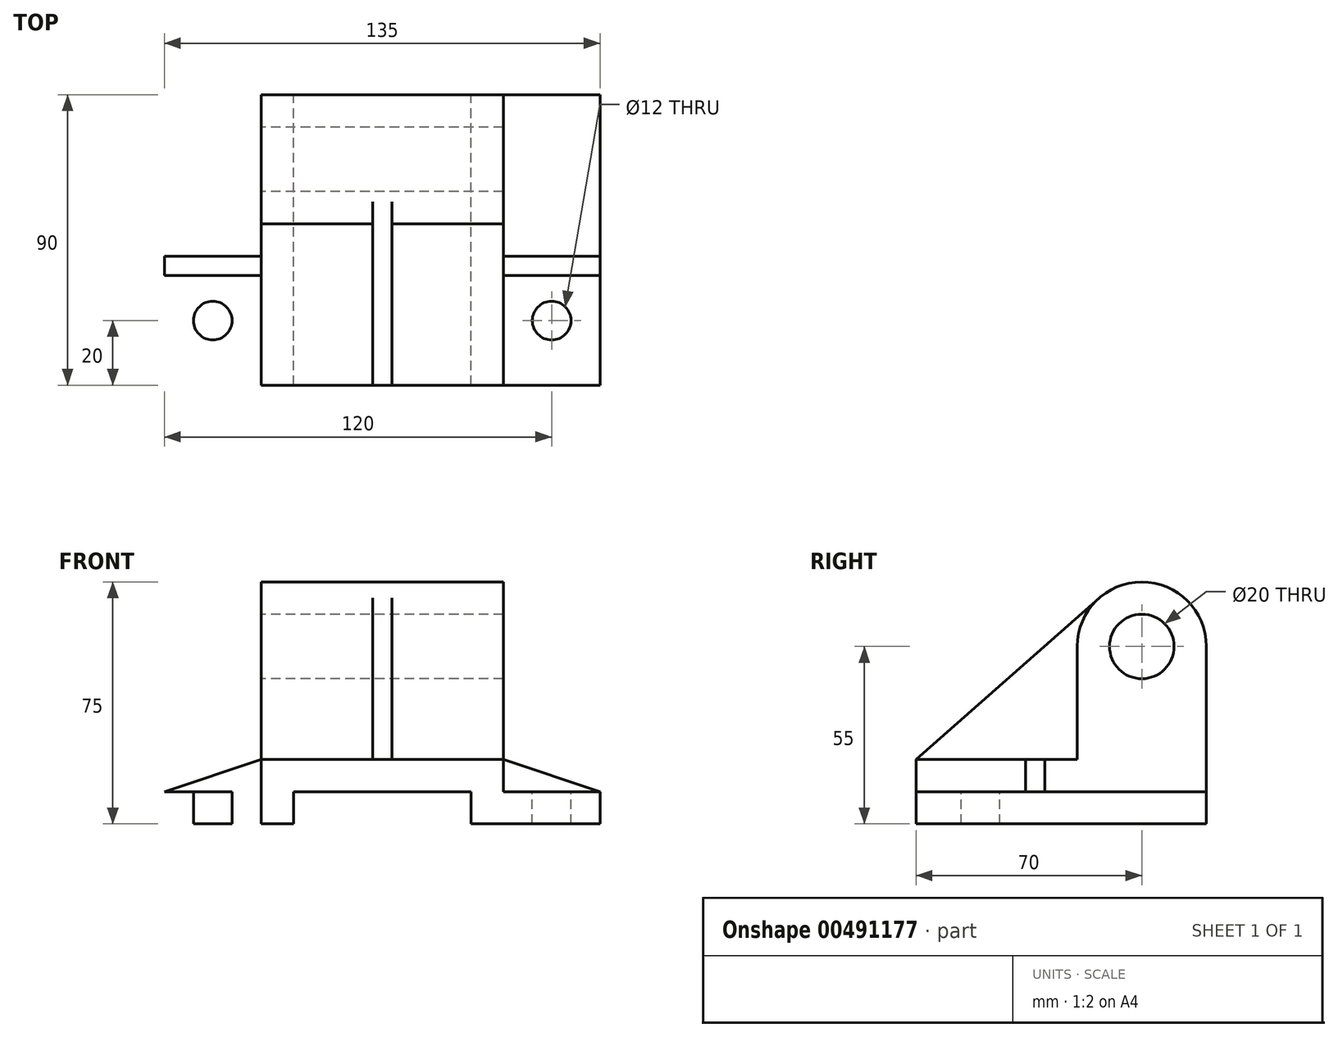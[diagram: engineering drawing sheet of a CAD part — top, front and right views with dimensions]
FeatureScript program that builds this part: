
annotation { "Feature Type Name" : "Feature", "Feature Type Description" : "" }
export const myFeature = defineFeature(function(context is Context, id is Id, definition is map)
    precondition{}
    {
        {
            var Q0;
            Q0=qCreatedBy(makeId("Front.planeOp"),FACE);
            var sketch = newSketch(context, id + "F0", { "sketchPlane" : qUnion([Q0])});
            skLineSegment(sketch, "E0", {"start": v(0, 10) * mm, "end": v(0, 20) * mm});
            skLineSegment(sketch, "E1", {"start": v(0, 20) * mm, "end": v(37.5, 20) * mm});
            skLineSegment(sketch, "E2", {"start": v(37.5, 20) * mm, "end": v(37.5, 10) * mm});
            skLineSegment(sketch, "E3", {"start": v(37.5, 10) * mm, "end": v(67.5, 10) * mm});
            skLineSegment(sketch, "E4", {"start": v(67.5, 10) * mm, "end": v(67.5, 0) * mm});
            skLineSegment(sketch, "E5", {"start": v(67.5, 0) * mm, "end": v(27.5, 0) * mm});
            skLineSegment(sketch, "E6", {"start": v(27.5, 0) * mm, "end": v(27.5, 10) * mm});
            skLineSegment(sketch, "E7", {"start": v(27.5, 10) * mm, "end": v(0, 10) * mm});
            skLineSegment(sketch, "E8.MirrorCS", {"start": v(0, 20) * mm, "end": v(-37.5, 20) * mm});
            skLineSegment(sketch, "E9.MirrorCS", {"start": v(-27.5, 10) * mm, "end": v(0, 10) * mm});
            skLineSegment(sketch, "E10.MirrorCS", {"start": v(-37.5, 20) * mm, "end": v(-37.5, 10) * mm});
            skLineSegment(sketch, "E11.MirrorCS", {"start": v(-27.5, 0) * mm, "end": v(-27.5, 10) * mm});
            skLineSegment(sketch, "E12.MirrorCS", {"start": v(-67.5, 0) * mm, "end": v(-27.5, 0) * mm});
            skLineSegment(sketch, "E13.MirrorCS", {"start": v(-37.5, 10) * mm, "end": v(-67.5, 10) * mm});
            skLineSegment(sketch, "E14.MirrorCS", {"start": v(-67.5, 10) * mm, "end": v(-67.5, 0) * mm});
            skSolve(sketch);
        }
        {
            var Q0;
            Q0 = qSketchRegion(id + "F0", true);
            extrude(context, id + "F1", {"entities" : qUnion([Q0]), "endBound" : BoundingType.SYMMETRIC, "depth" : 90 * mm});
        }
        {
            var Q0;
            Q0=makeQuery(id+"F1.opExtrude","SWEPT_FACE",FACE,{"disambiguationData":[OSD([sQuery(id+"F0.wireOp",EDGE,"E13.MirrorCS")])]});
            var sketch = newSketch(context, id + "F2", { "sketchPlane" : qUnion([Q0])});
            skCircle(sketch, "E15", {"center": v(-52.5, 25) * mm, "radius": 6 * mm});
            skCircle(sketch, "E16.MirrorC", {"center": v(52.5, 25) * mm, "radius": 6 * mm});
            skCircle(sketch, "E17.MirrorC", {"center": v(-52.5, -25) * mm, "radius": 6 * mm});
            skCircle(sketch, "E18.MirrorC", {"center": v(52.5, -25) * mm, "radius": 6 * mm});
            skSolve(sketch);
        }
        {
            var Q0;
            Q0=makeQuery(id+"F2.imprint","IMPRINT",FACE,{"disambiguationData":[TD([[makeQuery(id+"F2.imprint","IMPRINT",EDGE,{"derivedFrom":sQuery(id+"F2.wireOp",EDGE,"E15")}),1.0]])]});
            var Q1;
            Q1=makeQuery(id+"F2.imprint","IMPRINT",FACE,{"disambiguationData":[TD([[makeQuery(id+"F2.imprint","IMPRINT",EDGE,{"derivedFrom":sQuery(id+"F2.wireOp",EDGE,"E16.MirrorC")}),-1.0]])]});
            var Q2;
            Q2=makeQuery(id+"F2.imprint","IMPRINT",FACE,{"disambiguationData":[TD([[makeQuery(id+"F2.imprint","IMPRINT",EDGE,{"derivedFrom":sQuery(id+"F2.wireOp",EDGE,"E18.MirrorC")}),1.0]])]});
            var Q3;
            Q3=makeQuery(id+"F2.imprint","IMPRINT",FACE,{"disambiguationData":[TD([[makeQuery(id+"F2.imprint","IMPRINT",EDGE,{"derivedFrom":sQuery(id+"F2.wireOp",EDGE,"E17.MirrorC")}),-1.0]])]});
            var Q4;
            Q4=sQuery(id+"F2.wireOp",EDGE,"E15");
            var Q5;
            Q5=sQuery(id+"F2.wireOp",EDGE,"E16.MirrorC");
            var Q6;
            Q6=sQuery(id+"F2.wireOp",EDGE,"E18.MirrorC");
            var Q7;
            Q7=sQuery(id+"F2.wireOp",EDGE,"E17.MirrorC");
            extrude(context, id + "F3", {"entities" : qUnion([Q0, Q1, Q2, Q3]), "operationType" : NewBodyOperationType.REMOVE, "surfaceEntities" : qUnion([Q4, Q5, Q6, Q7]), "oppositeDirection" : true, "depth" : 25 * mm});
        }
        {
            var Q0;
            Q0=makeQuery(id+"F1.opExtrude","SWEPT_FACE",FACE,{"disambiguationData":[OSD([sQuery(id+"F0.wireOp",EDGE,"E10.MirrorCS")])]});
            var sketch = newSketch(context, id + "F4", { "sketchPlane" : qUnion([Q0])});
            skPoint(sketch, "E19.0", {"position": v(45, 20) * mm});
            skPoint(sketch, "E20.0", {"position": v(-45, 20) * mm});
            skLineSegment(sketch, "E21.0.0", {"start": v(-45, 20) * mm, "end": v(-45, 10) * mm, "construction": true});
            skLineSegment(sketch, "E21.0.1", {"start": v(-45, 10) * mm, "end": v(45, 10) * mm, "construction": true});
            skLineSegment(sketch, "E21.0.2", {"start": v(45, 10) * mm, "end": v(45, 20) * mm, "construction": true});
            skLineSegment(sketch, "E22", {"start": v(-45, 20) * mm, "end": v(45, 20) * mm});
            skLineSegment(sketch, "E23.0.3", {"start": v(45, 20) * mm, "end": v(-45, 20) * mm});
            skLineSegment(sketch, "E24", {"start": v(-45, 20) * mm, "end": v(-45, 55) * mm});
            skArc(sketch, "E25", {"start": v(-45, 55) * mm, "mid": v(-25, 75) * mm, "end": v(-5, 55) * mm});
            skLineSegment(sketch, "E26", {"start": v(-5, 55) * mm, "end": v(-5, 20) * mm});
            skCircle(sketch, "E27", {"center": v(-25, 55) * mm, "radius": 10 * mm});
            skSolve(sketch);
        }
        {
            var Q0;
            Q0 = qSketchRegion(id + "F4", true);
            var Q1;
            Q1=makeQuery(id+"F1.opExtrude","SWEPT_FACE",FACE,{"disambiguationData":[OSD([sQuery(id+"F0.wireOp",EDGE,"E2")])]});
            extrude(context, id + "F5", {"entities" : qUnion([Q0]), "operationType" : NewBodyOperationType.ADD, "endBound" : BoundingType.UP_TO_SURFACE, "oppositeDirection" : true, "endBoundEntityFace" : qUnion([Q1]), "depth" : 25 * mm});
        }
        {
            var Q0;
            Q0=qCreatedBy(makeId("Right.planeOp"),FACE);
            var sketch = newSketch(context, id + "F6", { "sketchPlane" : qUnion([Q0])});
            skPoint(sketch, "E28.0", {"position": v(25, 75) * mm});
            skPoint(sketch, "E29.0", {"position": v(-45, 20) * mm});
            skArc(sketch, "E30.0", {"start": v(45, 55) * mm, "mid": v(25, 75) * mm, "end": v(5, 55) * mm});
            skLineSegment(sketch, "E31.0.0", {"start": v(45, 10) * mm, "end": v(45, 55) * mm});
            skLineSegment(sketch, "E31.0.2", {"start": v(5, 55) * mm, "end": v(5, 20) * mm});
            skLineSegment(sketch, "E31.0.3", {"start": v(5, 20) * mm, "end": v(-45, 20) * mm});
            skLineSegment(sketch, "E31.0.4", {"start": v(-45, 20) * mm, "end": v(-45, 10) * mm});
            skLineSegment(sketch, "E31.0.5", {"start": v(-45, 10) * mm, "end": v(45, 10) * mm});
            skLineSegment(sketch, "E32.0.0", {"start": v(45, 10) * mm, "end": v(45, 55) * mm, "construction": true});
            skArc(sketch, "E32.0.1", {"start": v(45, 55) * mm, "mid": v(25, 75) * mm, "end": v(5, 55) * mm, "construction": true});
            skLineSegment(sketch, "E32.0.2", {"start": v(5, 55) * mm, "end": v(5, 20) * mm, "construction": true});
            skLineSegment(sketch, "E32.0.3", {"start": v(5, 20) * mm, "end": v(-45, 20) * mm, "construction": true});
            skLineSegment(sketch, "E32.0.4", {"start": v(-45, 20) * mm, "end": v(-45, 10) * mm, "construction": true});
            skLineSegment(sketch, "E32.0.5", {"start": v(-45, 10) * mm, "end": v(45, 10) * mm, "construction": true});
            skLineSegment(sketch, "E33", {"start": v(-45, 20) * mm, "end": v(11.78, 70) * mm});
            skSolve(sketch);
        }
        {
            var Q0;
            {var subQ0=sQuery(id+"F6.wireOp",EDGE,"E31.0.2");Q0=makeQuery(id+"F6.imprint","IMPRINT",FACE,{"disambiguationData":[TD([[makeQuery(id+"F6.imprint","IMPRINT",EDGE,{"derivedFrom":subQ0}),-1.0]])]});}
            extrude(context, id + "F7", {"entities" : qUnion([Q0]), "operationType" : NewBodyOperationType.ADD, "depth" : 3 * mm, "hasSecondDirection" : true, "secondDirectionOppositeDirection" : true, "secondDirectionDepth" : 3 * mm});
        }
        {
            var Q0;
            Q0=qCreatedBy(makeId("Front.planeOp"),FACE);
            cPlane(context, id + "F8", {"entities" : qUnion([Q0]), "cplaneType" : CPlaneType.OFFSET, "offset" : 5 * mm, "width" : 150 * mm, "height" : 150 * mm});
        }
        {
            var Q0;
            Q0=qCreatedBy(id+"F8.planeOp",FACE);
            var sketch = newSketch(context, id + "F9", { "sketchPlane" : qUnion([Q0])});
            skPoint(sketch, "E34.0", {"position": v(-37.5, 20) * mm});
            skPoint(sketch, "E35.0", {"position": v(-67.5, 10) * mm});
            skLineSegment(sketch, "E36", {"start": v(-67.5, 10) * mm, "end": v(-37.5, 20) * mm});
            skLineSegment(sketch, "E37.MirrorCS", {"start": v(67.5, 10) * mm, "end": v(37.5, 20) * mm});
            skPoint(sketch, "E38.0", {"position": v(-37.5, 15) * mm});
            skLineSegment(sketch, "E39.0", {"start": v(-37.5, 20) * mm, "end": v(-37.5, 10) * mm});
            skLineSegment(sketch, "E40.0", {"start": v(-37.5, 10) * mm, "end": v(-67.5, 10) * mm});
            skLineSegment(sketch, "E41.0", {"start": v(37.5, 20) * mm, "end": v(37.5, 10) * mm});
            skLineSegment(sketch, "E42.0", {"start": v(37.5, 10) * mm, "end": v(67.5, 10) * mm});
            skSolve(sketch);
        }
        {
            var Q0;
            Q0 = qSketchRegion(id + "F9", true);
            extrude(context, id + "F10", {"entities" : qUnion([Q0]), "operationType" : NewBodyOperationType.ADD, "depth" : 6 * mm});
        }
    });
